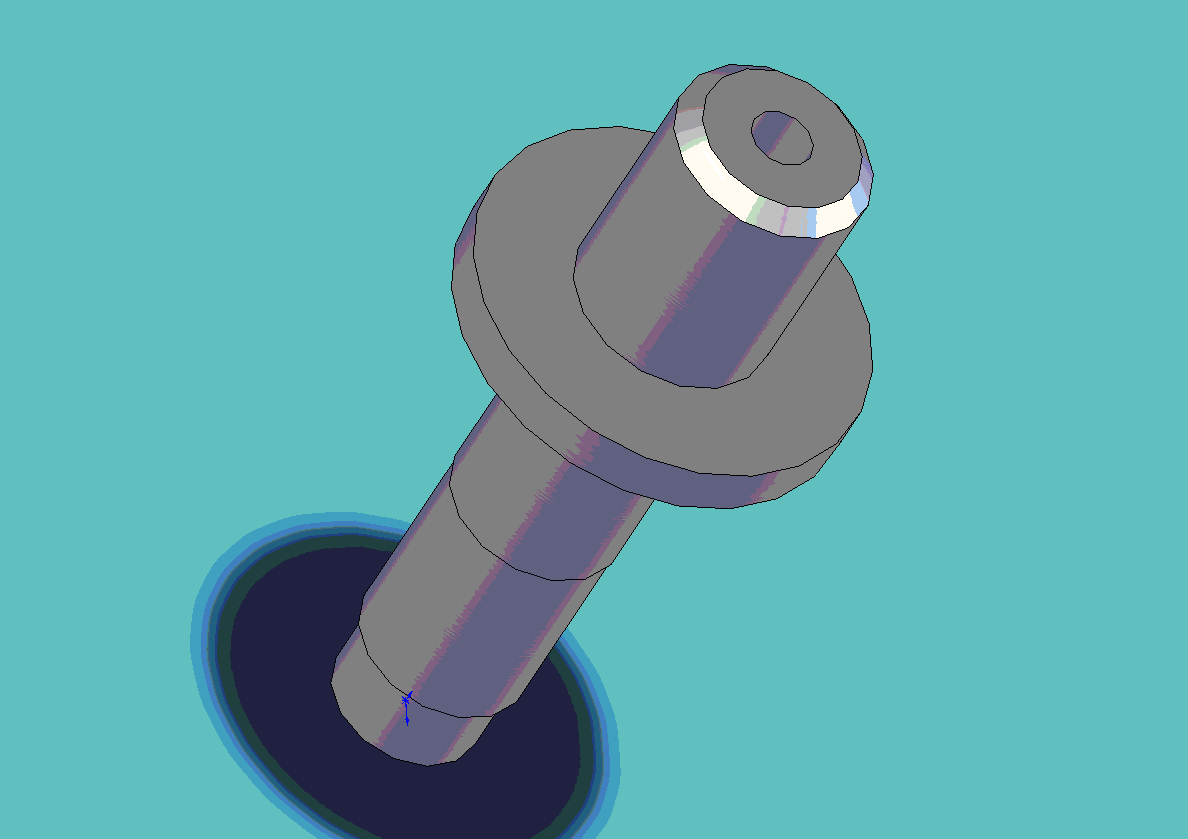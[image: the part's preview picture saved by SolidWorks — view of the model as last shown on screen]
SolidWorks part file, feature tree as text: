
SOLIDWORKS PART (.sldprt)
format: sldprt  version: not decoded by parser v0  size: 219,136 bytes
history: native  units: mm
features: sketch x4, cut_extrude x2, material x1, revolve x1, chamfer x1 (+13 scaffold rows collapsed)
feature tree (22):
  scaffold x13  (default folders/planes/origin — collapsed)
  material  "Titanium"
  sketch  "3DSketch4"  dims[c1.D13=5.08mm c1.D1=~16.54448mm c1.D5=9.525mm c1.D2=11.1125mm c1.D3=~23.13596mm c1.D4=~23.13596mm c2.D3=~25.116831mm c2.D5=~25.116831mm c2.D4=~23.13596mm c3.D5=~23.13596mm c3.D4=~25.116831mm c4.D5=~25.116831mm c4.D4=10.8712mm c4.D1=9.525mm c4.D3=~36.229331mm c4.D9=~36.229331mm c5.D5=11.1125mm c5.D6=12.7mm c5.D7=25.4mm c5.D8=~26.438545mm c5.D9=~26.438545mm c6.D8=12.7mm c6.D3=38.1mm c6.D9=65.024mm c6.D10=31.75mm c6.D11=6.35mm c6.D12=109.474mm c6.D13=65.024mm c6.D14=65.024mm]
  sketch  "Sketch4"  dims[c1.D15=5.08mm c1.D1=9.525mm c1.D2=10.8712mm c1.D3=11.1125mm c1.D4=12.7mm c1.D5=25.4mm c1.D6=12.7mm c1.D7=11.1125mm c1.D8=38.1mm c1.D9=65.024mm c1.D10=~186.360192mm c1.D11=31.75mm c1.D12=6.35mm c1.D13=109.474mm c2.D10=12.7mm c2.D14=6.35mm]
  revolve  "Revolve2"  Angle=360deg
  sketch  "Sketch5"  dims[D1=7.9375mm]
  cut_extrude  "Cut-Extrude1"  Depth=28.575mm
  sketch  "Sketch6"  dims[D1=7.9375mm]
  cut_extrude  "Cut-Extrude2"  Depth=33.782mm
  chamfer  "Chamfer1"  Distance=2.54mm Angle=45deg
decode coverage: 8 of 8 modeling features carry decoded parameters
note: ~ marks probable driven/reference dimensions
note: suppression state not decoded; provenance and decode notes live in map.json
